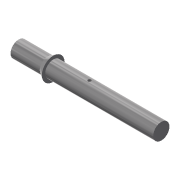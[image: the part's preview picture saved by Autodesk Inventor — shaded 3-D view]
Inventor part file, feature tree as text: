
AUTODESK INVENTOR PART (.ipt)
format: ipt  version: 2016 (Build 200138000, 138)  size: 169,984 bytes
history: native  units: mm
features: other x5, sketch x2, revolve x1, chamfer x1, extrude x1, projected_geometry x1
ambient origin geometry x6: Origin, XZ Plane, XY Plane, X Axis, Y Axis, Z Axis
bodies: Body1 (feature_tree)
feature tree (11):
  other  "Sólido1"
  revolve  "Revolución1"  [1 undecoded]
  other  "Ranura2"
  chamfer  "Chaflán3"  [1 undecoded]
  extrude  "Extrusión1"  Depth=3.0mm
  other  "Plano inicial"
  other  "Punto de origen"
  sketch  "Boceto principal"  dims[d4=15.0mm d5=0.0mm d14=3.0mm d15=33.6mm d16=40.0mm d17=0.0mm d19=0.5mm d20=0.125mm d21=45.0deg]
  sketch  "Boceto3"  dims[d0=0.0mm d1=0.0mm d2=0.0mm d3=15.0mm]
  projected_geometry  "Contorno proyectado1"
  other  "iFeature3:2"
note: 2 required parameter values undecoded (feature->parameter linkage not recoverable at this tier; creation-order binding heuristic only, values carry confidence <= 0.55)